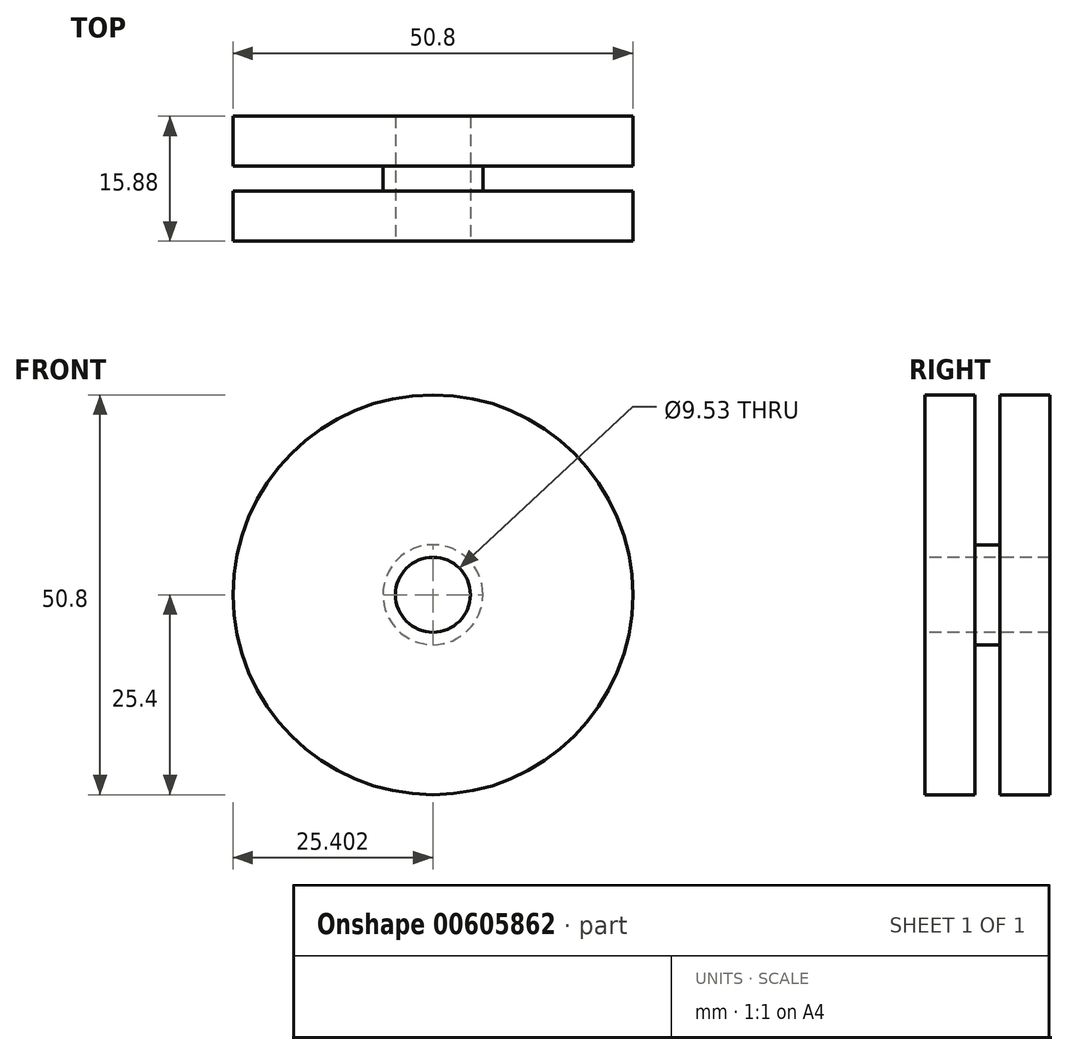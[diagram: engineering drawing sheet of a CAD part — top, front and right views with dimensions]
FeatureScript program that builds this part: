
annotation { "Feature Type Name" : "Feature", "Feature Type Description" : "" }
export const myFeature = defineFeature(function(context is Context, id is Id, definition is map)
    precondition{}
    {
        {
            var Q0;
            Q0=qCreatedBy(makeId("Front.planeOp"),FACE);
            var sketch = newSketch(context, id + "F0", { "sketchPlane" : qUnion([Q0])});
            skCircle(sketch, "E0", {"center": v(191.95, 0) * mm, "radius": 25.4 * mm});
            skCircle(sketch, "E1", {"center": v(191.95, 0) * mm, "radius": 4.76 * mm});
            skSolve(sketch);
        }
        {
            var Q0;
            Q0=makeQuery(id+"F0.imprint","IMPRINT",FACE,{"disambiguationData":[TD([[makeQuery(id+"F0.imprint","IMPRINT",EDGE,{"derivedFrom":sQuery(id+"F0.wireOp",EDGE,"E0")}),1.0]])]});
            extrude(context, id + "F1", {"entities" : qUnion([Q0]), "oppositeDirection" : true, "depth" : 6.35 * mm, "offsetDistance" : 25.4 * mm});
        }
        {
            var Q0;
            Q0=makeQuery(id+"F1.opExtrude","CAP_FACE",FACE,{"disambiguationData":[OSD([sQuery(id+"F0.wireOp",EDGE,"E0"),sQuery(id+"F0.wireOp",EDGE,"E1")])],"isStart":false});
            var sketch = newSketch(context, id + "F2", { "sketchPlane" : qUnion([Q0])});
            skCircle(sketch, "E2", {"center": v(-191.95, 0) * mm, "radius": 6.35 * mm});
            skSolve(sketch);
        }
        {
            var Q0;
            Q0=makeQuery(id+"F2.imprint","IMPRINT",FACE,{"disambiguationData":[TD([[makeQuery(id+"F2.imprint","IMPRINT",EDGE,{"derivedFrom":sQuery(id+"F2.wireOp",EDGE,"E2")}),1.0]])]});
            extrude(context, id + "F3", {"entities" : qUnion([Q0]), "operationType" : NewBodyOperationType.ADD, "depth" : 9.52 * mm, "offsetDistance" : 25.4 * mm});
        }
        {
            var Q0;
            Q0=makeQuery(id+"F3.opExtrude","CAP_FACE",FACE,{"disambiguationData":[OSD([sQuery(id+"F0.wireOp",EDGE,"E1"),sQuery(id+"F2.wireOp",EDGE,"E2")])],"isStart":false});
            var sketch = newSketch(context, id + "F4", { "sketchPlane" : qUnion([Q0])});
            skCircle(sketch, "E3", {"center": v(-191.95, 0) * mm, "radius": 25.4 * mm});
            skSolve(sketch);
        }
        {
            var Q0;
            Q0=makeQuery(id+"F4.imprint","IMPRINT",FACE,{"disambiguationData":[TD([[makeQuery(id+"F4.imprint","IMPRINT",EDGE,{"derivedFrom":sQuery(id+"F4.wireOp",EDGE,"E3")}),1.0]])]});
            extrude(context, id + "F5", {"entities" : qUnion([Q0]), "operationType" : NewBodyOperationType.ADD, "oppositeDirection" : true, "depth" : 6.35 * mm, "offsetDistance" : 25.4 * mm});
        }
    });
